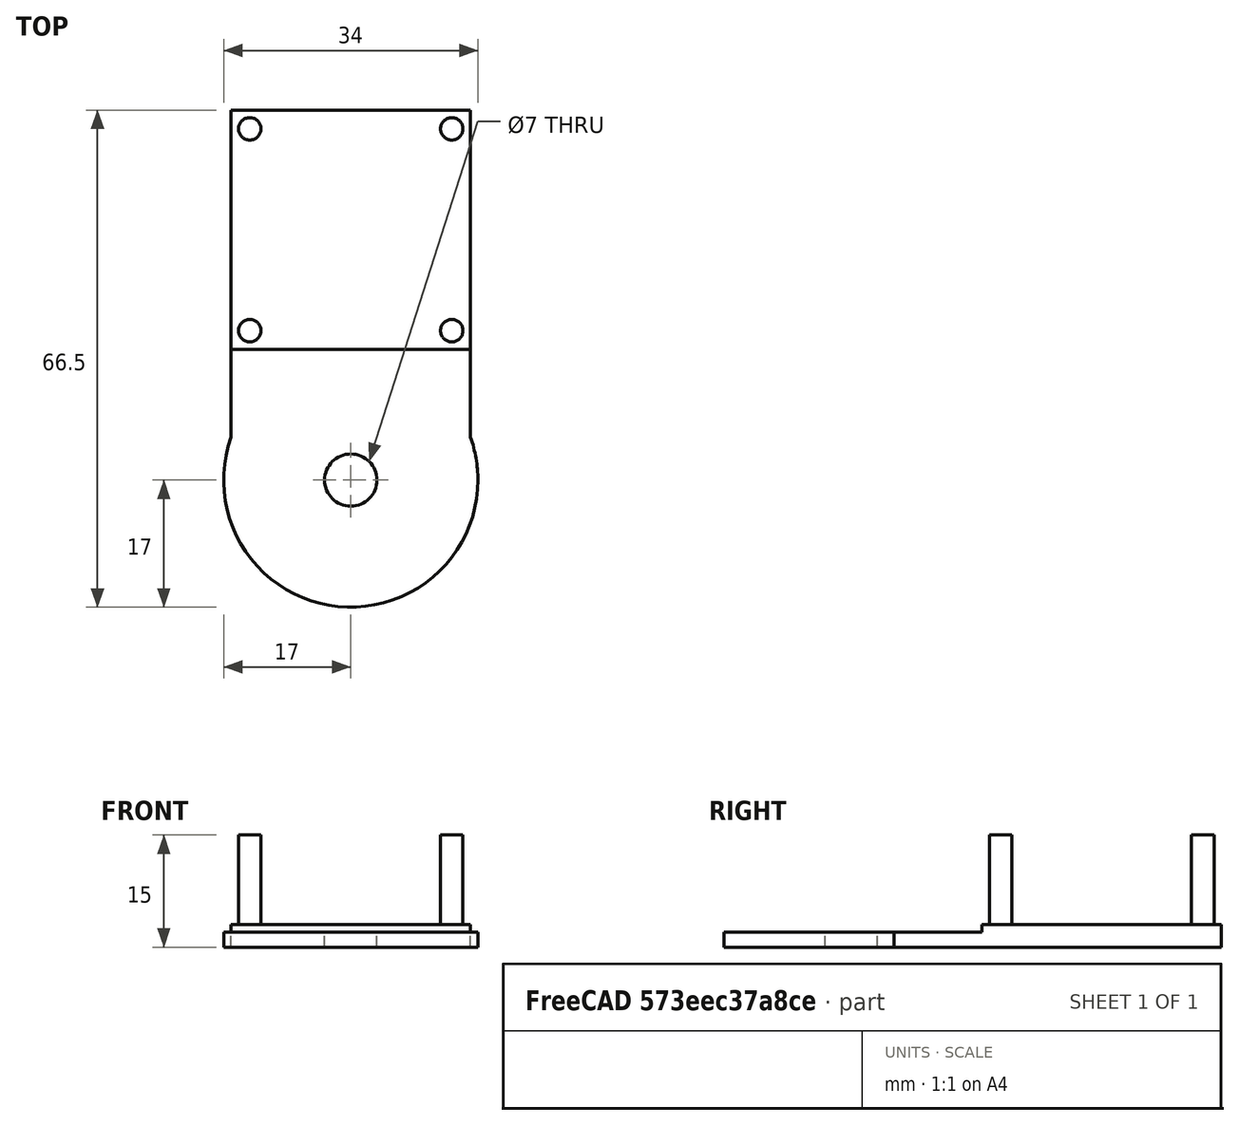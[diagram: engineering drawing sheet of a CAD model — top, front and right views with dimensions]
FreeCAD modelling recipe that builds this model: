
FCSTD DOCUMENT  (FreeCAD 0.17R13519 (Git))
Label: imu_holder_cad
License: All rights reserved
LicenseURL: http://en.wikipedia.org/wiki/All_rights_reserved
objects: Part::Cylinder×6, Part::Fuse×6, Part::Box×2, Part::Cut×1
note: 15 computed .brp shape members not serialized (recipe doc carries the construction recipe); baked Part::Feature solids carry a one-line shape summary decoded from their .brp

FEATURE [Part::Box] Box  label="Cube"
  AttacherType = Attacher::AttachEngine3D
  Height = 3
  Length = 32
  Width = 32
FEATURE [Part::Cylinder] Cylinder
  Angle = 360
  AttacherType = Attacher::AttachEngine3D
  Height = 15
  Placement = pos=(2.5,2.5,0) rot=(0,0,1;0rad)
  Radius = 1.5
FEATURE [Part::Cylinder] Cylinder001
  Angle = 360
  AttacherType = Attacher::AttachEngine3D
  Height = 15
  Placement = pos=(29.5,2.5,0) rot=(0,0,1;0rad)
  Radius = 1.5
FEATURE [Part::Cylinder] Cylinder002
  Angle = 360
  AttacherType = Attacher::AttachEngine3D
  Height = 15
  Placement = pos=(2.5,29.5,0) rot=(0,0,1;0rad)
  Radius = 1.5
FEATURE [Part::Cylinder] Cylinder003
  Angle = 360
  AttacherType = Attacher::AttachEngine3D
  Height = 15
  Placement = pos=(29.5,29.5,0) rot=(0,0,1;0rad)
  Radius = 1.5
FEATURE [Part::Fuse] Fusion
  Base = -> Box
  Tool = -> Cylinder
FEATURE [Part::Fuse] Fusion001
  Base = -> Fusion
  Tool = -> Cylinder001
FEATURE [Part::Fuse] Fusion002
  Base = -> Fusion001
  Tool = -> Cylinder002
FEATURE [Part::Fuse] Fusion003
  Base = -> Fusion002
  Tool = -> Cylinder003
FEATURE [Part::Cylinder] Cylinder004
  Angle = 360
  AttacherType = Attacher::AttachEngine3D
  Height = 2
  Placement = pos=(16,-17.5,0) rot=(0,0,1;0rad)
  Radius = 17
FEATURE [Part::Cylinder] Cylinder005
  Angle = 360
  AttacherType = Attacher::AttachEngine3D
  Height = 2
  Placement = pos=(16,-17.5,0) rot=(0,0,1;0rad)
  Radius = 3.5
FEATURE [Part::Cut] Cut
  Base = -> Cylinder004
  Tool = -> Cylinder005
FEATURE [Part::Box] Box001  label="Cube001"
  AttacherType = Attacher::AttachEngine3D
  Height = 2
  Length = 32
  Placement = pos=(0,-13,0) rot=(0,0,1;0rad)
  Width = 15
FEATURE [Part::Fuse] Fusion004
  Base = -> Fusion003
  Tool = -> Cut
FEATURE [Part::Fuse] Fusion005
  Base = -> Fusion004
  Tool = -> Box001
